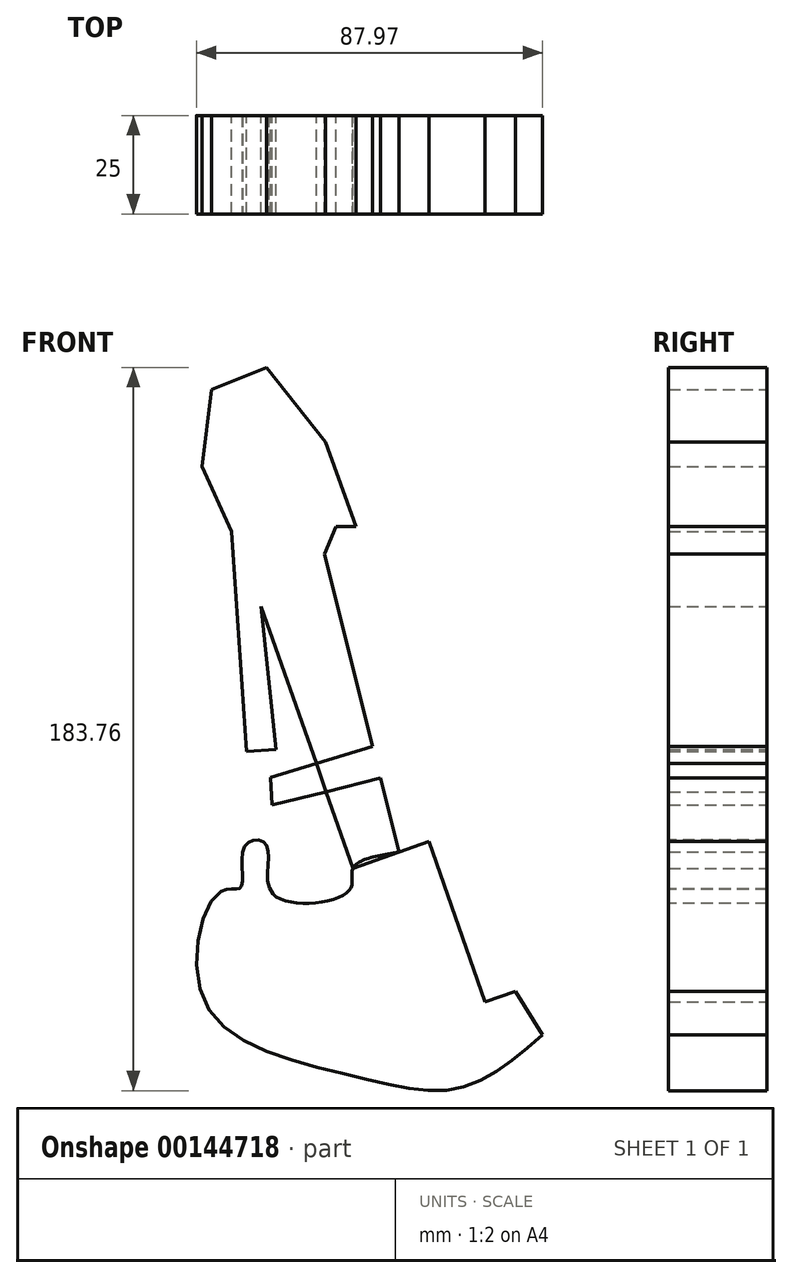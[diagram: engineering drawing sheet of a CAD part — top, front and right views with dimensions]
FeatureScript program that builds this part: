
annotation { "Feature Type Name" : "Feature", "Feature Type Description" : "" }
export const myFeature = defineFeature(function(context is Context, id is Id, definition is map)
    precondition{}
    {
        {
            var Q0;
            Q0=qCreatedBy(makeId("Front.planeOp"),FACE);
            var sketch = newSketch(context, id + "F0", { "sketchPlane" : qUnion([Q0])});
            skLineSegment(sketch, "E0", {"start": v(-62.86, 86.79) * mm, "end": v(-70.63, 108.22) * mm});
            skLineSegment(sketch, "E1", {"start": v(-70.63, 108.22) * mm, "end": v(-85.64, 127.25) * mm});
            skLineSegment(sketch, "E2", {"start": v(-85.64, 127.25) * mm, "end": v(-99.57, 121.62) * mm});
            skLineSegment(sketch, "E3", {"start": v(-99.57, 121.62) * mm, "end": v(-101.98, 102.06) * mm});
            skLineSegment(sketch, "E4", {"start": v(-101.98, 102.06) * mm, "end": v(-90.73, 77.14) * mm});
            skLineSegment(sketch, "E5", {"start": v(-90.73, 77.14) * mm, "end": v(-63.67, 0) * mm});
            skLineSegment(sketch, "E6", {"start": v(-63.67, 0) * mm, "end": v(-51.98, 4.1) * mm});
            skLineSegment(sketch, "E7", {"start": v(-51.98, 4.1) * mm, "end": v(-70.9, 79.82) * mm});
            skLineSegment(sketch, "E8", {"start": v(-70.9, 79.82) * mm, "end": v(-67.95, 86.79) * mm});
            skLineSegment(sketch, "E9", {"start": v(-67.95, 86.79) * mm, "end": v(-62.86, 86.79) * mm});
            skLineSegment(sketch, "E10", {"start": v(-94.5, 85.5) * mm, "end": v(-90.73, 29.72) * mm});
            skLineSegment(sketch, "E11", {"start": v(-90.73, 29.72) * mm, "end": v(-83.28, 30.22) * mm});
            skLineSegment(sketch, "E12", {"start": v(-83.28, 30.22) * mm, "end": v(-87, 66.51) * mm});
            skLineSegment(sketch, "E13", {"start": v(-89.64, 29.79) * mm, "end": v(-85.14, 30.1) * mm});
            skPoint(sketch, "E13.endSnap0", {"position": v(-85.14, 48.37) * mm});
            skLineSegment(sketch, "E14", {"start": v(-85.14, 30.1) * mm, "end": v(-84.19, 16.02) * mm});
            skLineSegment(sketch, "E15", {"start": v(-84.19, 16.02) * mm, "end": v(-87.92, 15.77) * mm});
            skLineSegment(sketch, "E16", {"start": v(-87.92, 15.77) * mm, "end": v(-89.64, 29.79) * mm});
            skLineSegment(sketch, "E17", {"start": v(-84.19, 16.02) * mm, "end": v(-56.68, 22.9) * mm});
            skLineSegment(sketch, "E18", {"start": v(-56.68, 22.9) * mm, "end": v(-58.68, 30.9) * mm});
            skLineSegment(sketch, "E19", {"start": v(-58.68, 30.9) * mm, "end": v(-84.66, 23.06) * mm});
            skLineSegment(sketch, "E20", {"start": v(-51.98, 4.1) * mm, "end": v(-44.41, 6.76) * mm});
            skLineSegment(sketch, "E21", {"start": v(-44.41, 6.76) * mm, "end": v(-30.11, -34) * mm});
            skLineSegment(sketch, "E22", {"start": v(-30.11, -34) * mm, "end": v(-22.42, -31.3) * mm});
            skLineSegment(sketch, "E23", {"start": v(-22.42, -31.3) * mm, "end": v(-15.48, -42.29) * mm});
            skFitSpline(sketch, "E24", {"points": [v(-15.48, -42.29) * mm, v(-36.41, -55.79) * mm, v(-65.11, -52.41) * mm, v(-101.57, -33.5) * mm, v(-97.18, -5.83) * mm, v(-92.12, -4.81) * mm, v(-91.1, 5.65) * mm, v(-85.7, 6) * mm, v(-84.02, -6.5) * mm, v(-64.77, -5.83) * mm, v(-63.67, 0) * mm, v(-51.98, 4.1) * mm], "startDerivative": vector(-176.61, -153.17) * mm, "endDerivative": vector(198.3, 32.1) * mm});
            skLineSegment(sketch, "E25", {"start": v(-97.18, -5.83) * mm, "end": v(-89.64, 29.79) * mm});
            skLineSegment(sketch, "E26", {"start": v(-84.19, 16.02) * mm, "end": v(-84.02, -6.5) * mm});
            skLineSegment(sketch, "E27", {"start": v(-66.78, 113.83) * mm, "end": v(-85.64, 127.25) * mm});
            skSolve(sketch);
        }
        {
            var Q0;
            Q0=makeQuery(id+"F0.imprint","IMPRINT",FACE,{"disambiguationData":[TD([[makeQuery(id+"F0.imprint","IMPRINT",EDGE,{"derivedFrom":sQuery(id+"F0.wireOp",EDGE,"E0")}),1.0]])]});
            var Q1;
            {var subQ0=sQuery(id+"F0.wireOp",EDGE,"E6");Q1=makeQuery(id+"F0.imprint","IMPRINT",FACE,{"disambiguationData":[TD([[makeQuery(id+"F0.imprint","IMPRINT",EDGE,{"derivedFrom":subQ0}),-1.0]])]});}
            var Q2;
            {var subQ2=sQuery(id+"F0.wireOp",EDGE,"E5");var subQ4=sQuery(id+"F0.wireOp",EDGE,"E17");var subQ5=makeQuery(id+"F0.imprint","INTERSECT",VERTEX,{"derivedFrom":[subQ2,subQ4]});Q2=makeQuery(id+"F0.imprint","IMPRINT",FACE,{"disambiguationData":[TD([[makeQuery(id+"F0.imprint","IMPRINT",EDGE,{"disambiguationData":[TD([[subQ5,-1.0]])],"derivedFrom":subQ2}),1.0]])]});}
            var Q3;
            {var subQ5=sQuery(id+"F0.wireOp",EDGE,"E18");Q3=makeQuery(id+"F0.imprint","IMPRINT",FACE,{"disambiguationData":[TD([[makeQuery(id+"F0.imprint","IMPRINT",EDGE,{"derivedFrom":subQ5}),1.0]])]});}
            var Q4;
            {var subQ0=sQuery(id+"F0.wireOp",EDGE,"E19");var subQ1=sQuery(id+"F0.wireOp",EDGE,"E5");var subQ2=makeQuery(id+"F0.imprint","INTERSECT",VERTEX,{"derivedFrom":[subQ1,subQ0]});Q4=makeQuery(id+"F0.imprint","IMPRINT",FACE,{"disambiguationData":[TD([[makeQuery(id+"F0.imprint","IMPRINT",EDGE,{"disambiguationData":[TD([[subQ2,-1.0]])],"derivedFrom":subQ1}),-1.0]])]});}
            var Q5;
            {var subQ3=sQuery(id+"F0.wireOp",EDGE,"E13");Q5=makeQuery(id+"F0.imprint","IMPRINT",FACE,{"disambiguationData":[TD([[makeQuery(id+"F0.imprint","IMPRINT",EDGE,{"derivedFrom":subQ3}),-1.0]])]});}
            var Q6;
            {var subQ1=sQuery(id+"F0.wireOp",EDGE,"E10");Q6=makeQuery(id+"F0.imprint","IMPRINT",FACE,{"disambiguationData":[TD([[makeQuery(id+"F0.imprint","IMPRINT",EDGE,{"derivedFrom":subQ1}),1.0]])]});}
            extrude(context, id + "F1", {"entities" : qUnion([Q0, Q1, Q2, Q3, Q4, Q5, Q6]), "depth" : 25 * mm});
        }
    });
